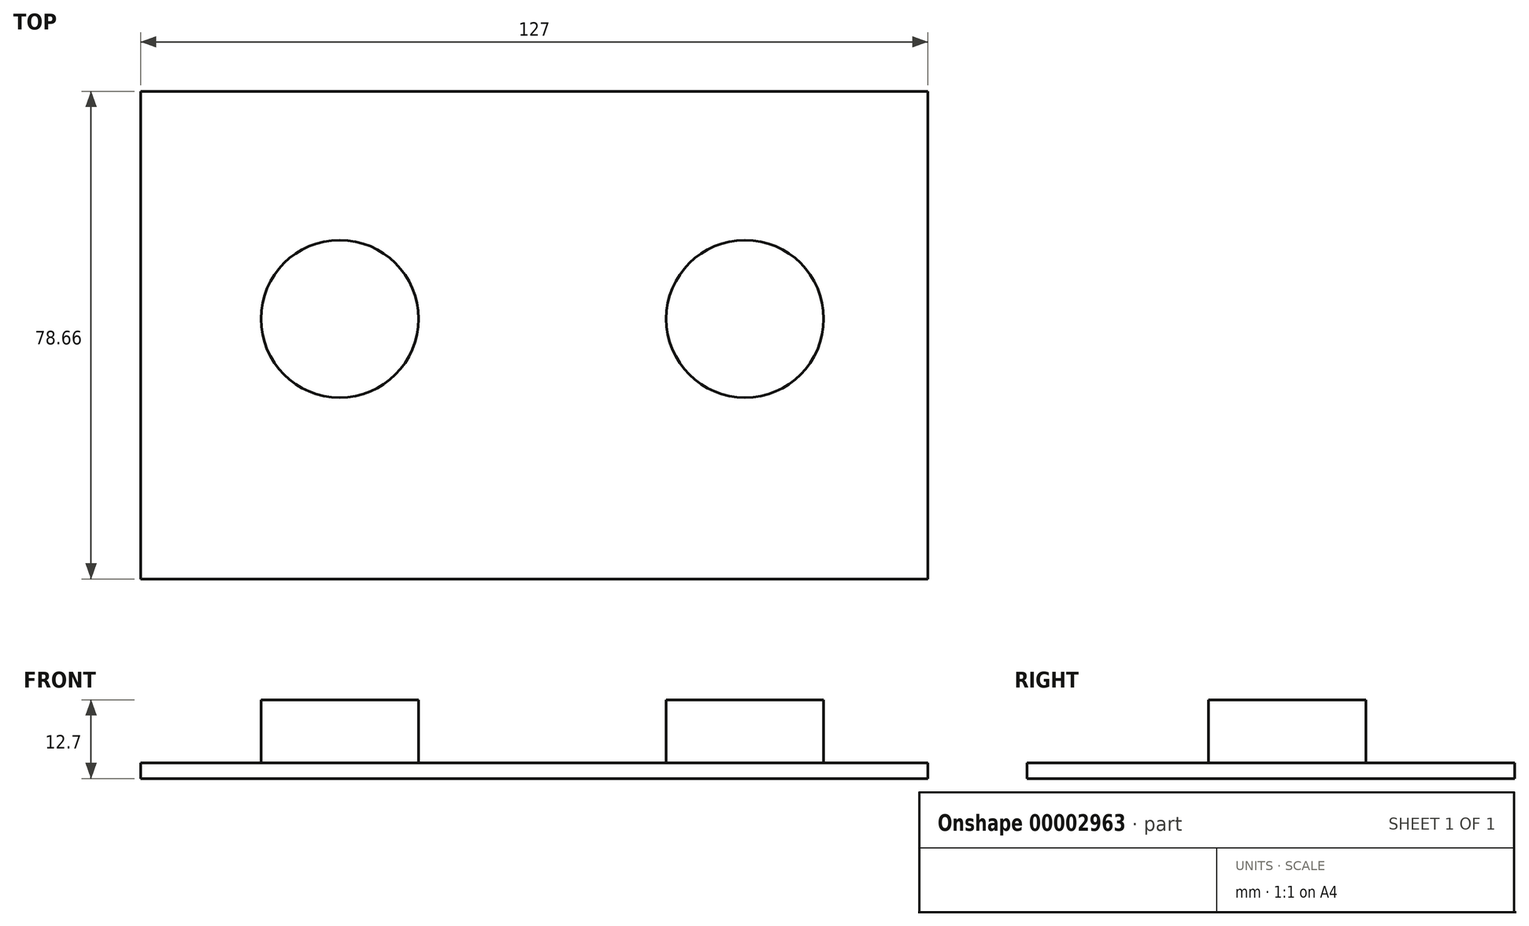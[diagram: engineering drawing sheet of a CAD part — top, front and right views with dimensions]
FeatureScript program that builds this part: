
annotation { "Feature Type Name" : "Feature", "Feature Type Description" : "" }
export const myFeature = defineFeature(function(context is Context, id is Id, definition is map)
    precondition{}
    {
        {
            var Q0;
            Q0=qCreatedBy(makeId("Top.planeOp"),FACE);
            var sketch = newSketch(context, id + "F0", { "sketchPlane" : qUnion([Q0])});
            skLineSegment(sketch, "E0.bottom", {"start": v(-71.6, 36.7) * mm, "end": v(55.4, 36.7) * mm});
            skLineSegment(sketch, "E0.top", {"start": v(-71.6, -41.96) * mm, "end": v(55.4, -41.96) * mm});
            skLineSegment(sketch, "E0.left", {"start": v(-71.6, 36.7) * mm, "end": v(-71.6, -41.96) * mm});
            skLineSegment(sketch, "E0.right", {"start": v(55.4, 36.7) * mm, "end": v(55.4, -41.96) * mm});
            skSolve(sketch);
        }
        {
            var Q0;
            Q0=makeQuery(id+"F0.imprint","IMPRINT",FACE,{"disambiguationData":[TD([[makeQuery(id+"F0.imprint","IMPRINT",EDGE,{"derivedFrom":sQuery(id+"F0.wireOp",EDGE,"E0.bottom")}),-1.0]])]});
            extrude(context, id + "F1", {"entities" : qUnion([Q0]), "depth" : 2.54 * mm});
        }
        {
            var Q0;
            Q0=makeQuery(id+"F1.opExtrude","CAP_FACE",FACE,{"disambiguationData":[OSD([sQuery(id+"F0.wireOp",EDGE,"E0.bottom"),sQuery(id+"F0.wireOp",EDGE,"E0.top"),sQuery(id+"F0.wireOp",EDGE,"E0.left"),sQuery(id+"F0.wireOp",EDGE,"E0.right")])],"isStart":false});
            var sketch = newSketch(context, id + "F2", { "sketchPlane" : qUnion([Q0])});
            skCircle(sketch, "E1", {"center": v(-39.48, 0) * mm, "radius": 12.7 * mm});
            skCircle(sketch, "E2", {"center": v(25.9, 0) * mm, "radius": 12.7 * mm});
            skSolve(sketch);
        }
        {
            var Q0;
            Q0=makeQuery(id+"F2.imprint","IMPRINT",FACE,{"disambiguationData":[TD([[makeQuery(id+"F2.imprint","IMPRINT",EDGE,{"derivedFrom":sQuery(id+"F2.wireOp",EDGE,"E1")}),1.0]])]});
            var Q1;
            Q1=makeQuery(id+"F2.imprint","IMPRINT",FACE,{"disambiguationData":[TD([[makeQuery(id+"F2.imprint","IMPRINT",EDGE,{"derivedFrom":sQuery(id+"F2.wireOp",EDGE,"E2")}),1.0]])]});
            extrude(context, id + "F3", {"entities" : qUnion([Q0, Q1]), "operationType" : NewBodyOperationType.ADD, "depth" : 10.16 * mm});
        }
    });
